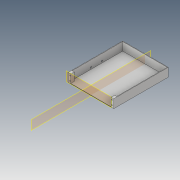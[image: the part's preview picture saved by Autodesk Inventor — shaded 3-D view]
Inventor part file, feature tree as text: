
AUTODESK INVENTOR PART (.ipt)
format: ipt  version: 2019 (Build 230136000, 136)  size: 184,320 bytes
history: native  units: mm
features: sketch x9, extrude x5, hole x4, plane x2, mirror x1, projected_geometry x1
ambient origin geometry x8: Origin, YZ Plane, XZ Plane, XY Plane, X Axis, Y Axis, Z Axis, Center Point
bodies: Solid1 (feature_tree)
feature tree (22):
  sketch  "Sketch1"  dims[d0=295.0mm d1=105.0mm]
  sketch  "Sketch2"  dims[d2=7.6mm d3=3.0mm]
  extrude  "Extrusion1"  Depth=105.0mm
  extrude  "Extrusion2"  Depth=3.0mm
  extrude  "Extrusion4"  Depth=1.0mm TaperAngle=0.0deg
  extrude  "Extrusion6"  Depth=1.0mm
  plane  "Work Plane2"
  plane  "Work Plane4"
  hole  "Hole3"  [1 undecoded]
  hole  "Hole4"  [1 undecoded]
  hole  "Hole5"  [1 undecoded]
  hole  "Hole6"  [1 undecoded]
  mirror  "Mirror6"
  extrude  "Extrusion12"  TaperAngle=150.0deg  [1 undecoded]
  sketch  "Sketch5"  dims[d4=14.0mm d7=1.0mm d8=0.0mm]
  sketch  "Sketch7"  dims[d9=23.0mm d10=1.0mm d11=0.0mm d12=0.0mm d35=4.5mm]
  projected_geometry  "Projected Loop4"
  sketch  "Sketch16"  dims[d37=4.5mm d39=4.5mm]
  sketch  "Sketch17"  dims[d40=0.0mm d41=30.8mm]
  sketch  "Sketch18"  dims[d45=4.5mm d46=0.0mm]
  sketch  "Sketch19"  dims[d47=30.8mm d50=10.0mm d51=0.0mm]
  sketch  "Sketch21"  dims[d57=135.0deg d58=135.0deg d61=6.0mm d62=0.0mm d64=150.0deg d65=150.0deg d71=10.0mm d72=4.0mm d73=10.0mm d74=4.0mm d75=1.5mm d76=60.0mm d77=60.0mm d106=10.0mm d107=10.0mm d108=3.5mm d109=5.0mm d110=2.6mm d111=6.0mm d112=5.0mm d113=2.0mm d114=14.3117mm d115=5.0mm d116=0.0mm d117=2.6mm d118=6.0mm d119=5.0mm d120=2.0mm d121=14.3117mm d122=15.0mm d123=20.594885mm d124=3.5mm d125=5.0mm d126=2.6mm d127=6.0mm d128=5.0mm d129=2.0mm d130=14.3117mm d131=5.0mm d132=0.0mm d133=2.6mm d134=6.0mm d135=5.0mm d136=2.0mm d137=14.3117mm d138=15.0mm d139=20.594885mm d142=5.2mm d143=0.0mm d144=18.0mm d145=18.0mm d148=151.5mm d149=151.5mm d91=1.0mm d92=1.0mm d93=1.0mm d94=0.15mm d95=0.25mm d96=0.375mm d97=14.3117mm d98=0.75mm d99=20.594885mm d100=0.0625mm d101=0.75mm d102=0.375mm]
note: 5 required parameter values undecoded (feature->parameter linkage not recoverable at this tier; creation-order binding heuristic only, values carry confidence <= 0.55)
